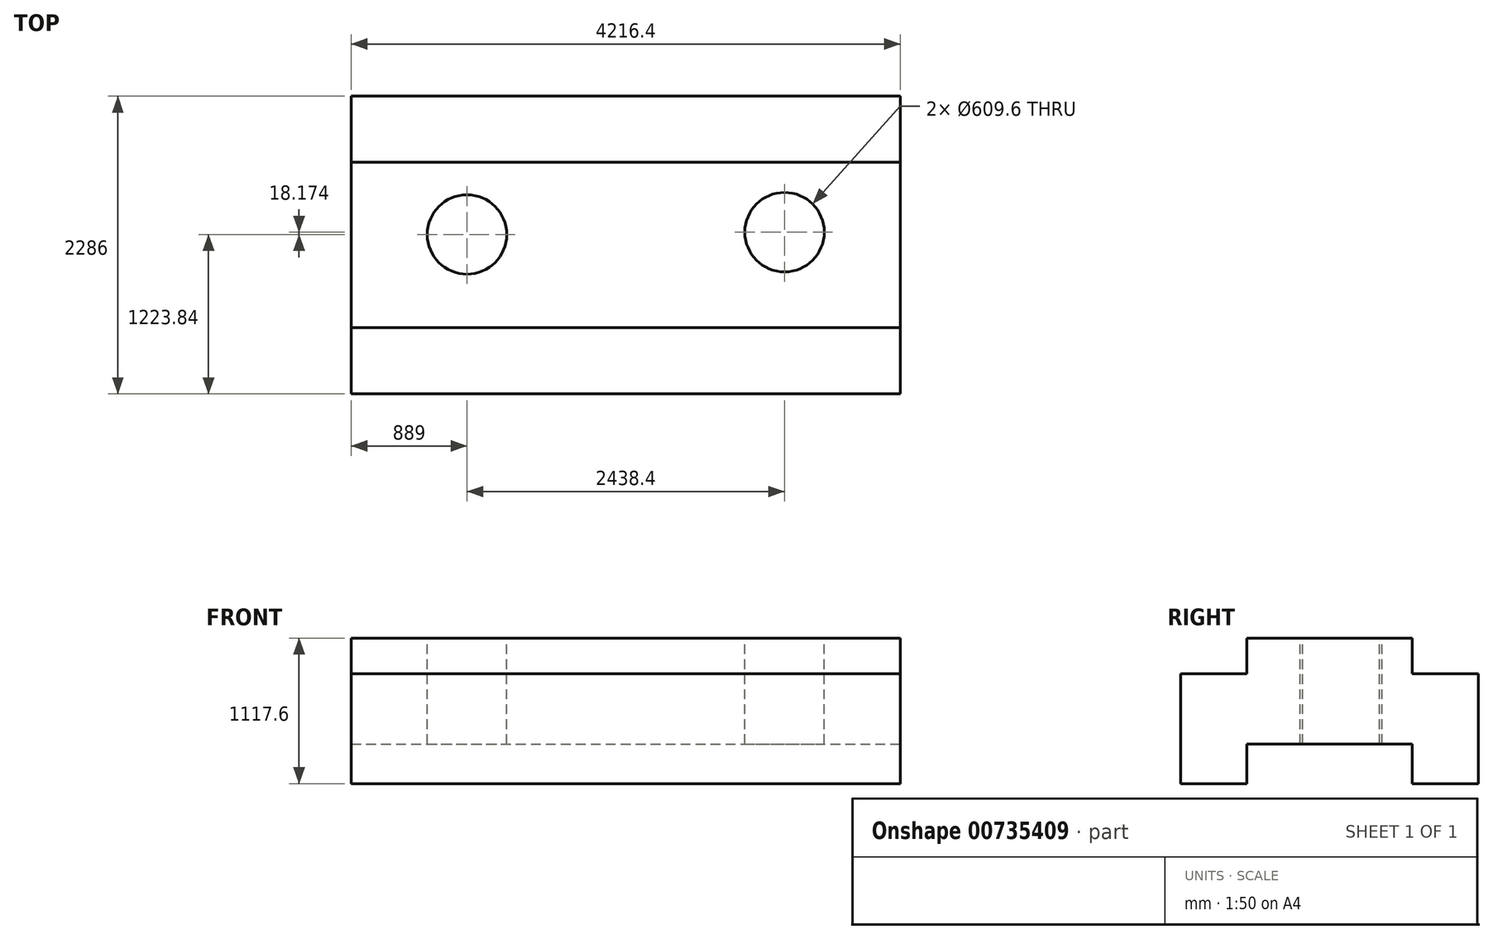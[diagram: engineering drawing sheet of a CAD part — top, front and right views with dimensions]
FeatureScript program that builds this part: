
annotation { "Feature Type Name" : "Feature", "Feature Type Description" : "" }
export const myFeature = defineFeature(function(context is Context, id is Id, definition is map)
    precondition{}
    {
        {
            var Q0;
            Q0=qCreatedBy(makeId("Right.planeOp"),FACE);
            var sketch = newSketch(context, id + "F0", { "sketchPlane" : qUnion([Q0])});
            skLineSegment(sketch, "E0.bottom", {"start": v(-2244.25, 1120.5) * mm, "end": v(41.75, 1120.5) * mm});
            skLineSegment(sketch, "E0.top", {"start": v(-2244.25, 2.9) * mm, "end": v(41.75, 2.9) * mm});
            skLineSegment(sketch, "E0.left", {"start": v(-2244.25, 1120.5) * mm, "end": v(-2244.25, 2.9) * mm});
            skLineSegment(sketch, "E0.right", {"start": v(41.75, 1120.5) * mm, "end": v(41.75, 2.9) * mm});
            skLineSegment(sketch, "E1.bottom", {"start": v(-1736.25, 307.7) * mm, "end": v(-466.25, 307.7) * mm});
            skLineSegment(sketch, "E1.top", {"start": v(-1736.25, 2.9) * mm, "end": v(-466.25, 2.9) * mm});
            skLineSegment(sketch, "E1.left", {"start": v(-1736.25, 307.7) * mm, "end": v(-1736.25, 2.9) * mm});
            skLineSegment(sketch, "E1.right", {"start": v(-466.25, 307.7) * mm, "end": v(-466.25, 2.9) * mm});
            skLineSegment(sketch, "E2.bottom", {"start": v(41.75, 1120.5) * mm, "end": v(-466.25, 1120.5) * mm});
            skLineSegment(sketch, "E2.top", {"start": v(41.75, 846.57) * mm, "end": v(-466.25, 846.57) * mm});
            skLineSegment(sketch, "E2.left", {"start": v(41.75, 1120.5) * mm, "end": v(41.75, 846.57) * mm});
            skLineSegment(sketch, "E2.right", {"start": v(-466.25, 1120.5) * mm, "end": v(-466.25, 846.57) * mm});
            skLineSegment(sketch, "E3.bottom", {"start": v(-2244.25, 1120.5) * mm, "end": v(-1736.25, 1120.5) * mm});
            skLineSegment(sketch, "E3.top", {"start": v(-2244.25, 846.57) * mm, "end": v(-1736.25, 846.57) * mm});
            skLineSegment(sketch, "E3.left", {"start": v(-2244.25, 1120.5) * mm, "end": v(-2244.25, 846.57) * mm});
            skLineSegment(sketch, "E3.right", {"start": v(-1736.25, 1120.5) * mm, "end": v(-1736.25, 846.57) * mm});
            skSolve(sketch);
        }
        {
            var Q0;
            Q0=makeQuery(id+"F0.imprint","IMPRINT",FACE,{"disambiguationData":[TD([[makeQuery(id+"F0.imprint","IMPRINT",EDGE,{"derivedFrom":sQuery(id+"F0.wireOp",EDGE,"E1.bottom")}),1.0]])]});
            extrude(context, id + "F1", {"entities" : qUnion([Q0]), "oppositeDirection" : true, "depth" : 4216.4 * mm, "offsetDistance" : 25.4 * mm});
        }
        {
            var Q0;
            Q0=makeQuery(id+"F1.opExtrude","SWEPT_FACE",FACE,{"disambiguationData":[OSD([sQuery(id+"F0.wireOp",EDGE,"E0.bottom")])]});
            var sketch = newSketch(context, id + "F2", { "sketchPlane" : qUnion([Q0])});
            skCircle(sketch, "E4", {"center": v(-3327.4, -1020.42) * mm, "radius": 304.8 * mm});
            skCircle(sketch, "E5", {"center": v(-889, -1002.24) * mm, "radius": 304.8 * mm});
            skSolve(sketch);
        }
        {
            var Q0;
            Q0=makeQuery(id+"F2.imprint","IMPRINT",FACE,{"disambiguationData":[TD([[makeQuery(id+"F2.imprint","IMPRINT",EDGE,{"derivedFrom":sQuery(id+"F2.wireOp",EDGE,"E4")}),1.0]])]});
            var Q1;
            Q1=makeQuery(id+"F2.imprint","IMPRINT",FACE,{"disambiguationData":[TD([[makeQuery(id+"F2.imprint","IMPRINT",EDGE,{"derivedFrom":sQuery(id+"F2.wireOp",EDGE,"E5")}),1.0]])]});
            extrude(context, id + "F3", {"entities" : qUnion([Q0, Q1]), "operationType" : NewBodyOperationType.REMOVE, "oppositeDirection" : true, "depth" : 1270 * mm, "offsetDistance" : 25.4 * mm});
        }
    });
